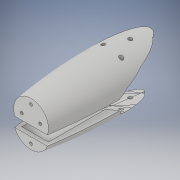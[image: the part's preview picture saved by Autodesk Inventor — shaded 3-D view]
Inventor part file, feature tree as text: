
AUTODESK INVENTOR PART (.ipt)
format: ipt  version: 2017 (Build 210142000, 142)  size: 2,322,432 bytes
history: native  units: in
note: dims shown in document units (in); Inventor stores cm internally (conversion verified against a paired STEP export)
features: reference x14, sketch x6, other x6, plane x5, projected_geometry x5, extrude x4, loft x1, surface_op x1, split x1, move_body x1
ambient origin geometry x8: Origin, YZ Plane, XZ Plane, XY Plane, X Axis, Y Axis, Z Axis, Center Point
bodies: Solid2 (feature_tree), Solid3 (feature_tree), Solid4 (feature_tree)
feature tree (44):
  plane  "Work Plane5"
  extrude  "Extrusion3"  Depth=1.4173in
  plane  "Work Plane7"
  loft  "Loft2"
  surface_op  "Sculpt1"
  extrude  "Extrusion5"  Depth=0.1181in
  extrude  "Extrusion4"  TaperAngle=90.0deg  [1 undecoded]
  plane  "Work Plane8"
  extrude  "Extrusion8"  Depth=0.315in TaperAngle=0.0deg
  plane  "Work Plane9"
  split  "Split1"
  move_body  "Move Body1"
  sketch  "Sketch5"  dims[d21=2.5in d22=1.4173in]
  reference  "Reference17"
  reference  "Reference18"
  reference  "Reference19"
  reference  "Reference20"
  reference  "Reference21"
  reference  "Reference22"
  reference  "Reference23"
  reference  "Reference24"
  reference  "Reference25"
  reference  "Reference26"
  reference  "Reference27"
  reference  "Reference28"
  reference  "Reference29"
  reference  "Reference30"
  plane  "Work Plane6"
  sketch  "Sketch6"  dims[d23=0.9843in d24=0.1181in]
  sketch  "Sketch7"  dims[d25=0.1181in d26=0.1181in]
  other  "Edges2"
  sketch  "Sketch9"  dims[d27=0.1181in d28=90.0deg]
  projected_geometry  "Projected Loop2"
  sketch  "Sketch10"  dims[d29=0.748in d30=0.315in d31=0.0in]
  projected_geometry  "Projected Loop3"
  sketch  "Sketch14"  dims[d32=2.5in d33=2.9375in d34=0.0in d35=90.0deg d36=0.0in d37=90.0deg d38=0.0in d39=90.0deg d40=0.9843in d41=0.748in d42=0.1181in d43=0.1181in d44=0.1181in d45=0.1181in d46=0.4975in d47=0.0in d48=0.1575in d50=3.9562in d51=0.0in d62=-3.4375in d63=6.5438in d64=0.0in d65=0.1575in d66=0.1575in d67=0.0in d68=0.0in d69=0.3937in d70=0.0in]
  projected_geometry  "Projected Loop4"
  projected_geometry  "Projected Loop5"
  projected_geometry  "Projected Loop6"
  other  "<userpath>\Desktop\asa1\assembly.iam"
  other  "assembly.iam"
  other  "Part1:1"
  other  "Composite1"
  other  "Srf1"
note: 1 required parameter value undecoded (feature->parameter linkage not recoverable at this tier; creation-order binding heuristic only, values carry confidence <= 0.55)
